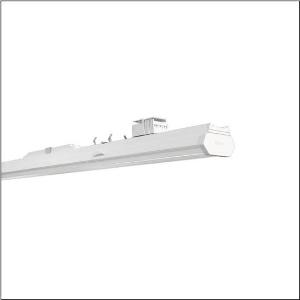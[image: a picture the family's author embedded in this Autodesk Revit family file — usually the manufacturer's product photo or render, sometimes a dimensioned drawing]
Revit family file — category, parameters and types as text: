
# Revit family: licross_11_protected_ho_51tp11cn4exs
name_source: partatom
category: Lighting Fixtures
units: mm (PartAtom-declared; Revit-internal decimal feet)

## family parameters
Cut with Voids When Loaded = No
Host = Face
Light Source = No
Part Type = Normal
Room Calculation Point = No
Round Connector Dimension = Use Diameter
Shared = No

## types (1)
- --- (1 x LED, 14460 lm, 77.6 W, 4000K)
    Apparent Load = 78 VA
    CIE Flux Codes = 84 94 98 99 100
    Color Rendering = 80
    Color Temperature = 4000K
    Default Elevation = 1800 mm
    Description = Licross 11 Protected HO, luminaire insert, of sheet steel, galvanised, coil coated, white, length: 1.500mm, width: 90mm, height: 101mm, LED rated luminous flux: 14.460lm, light colour: 840, SDCM (Standard Deviation of Colour Matching)MacAdam ≤ 2 SDCM (initial), control gear: ON/OFF Multilumen, CLOi, with plug, 3-pole, with phase selection, mains connection: 220..240V, AC, 50/60Hz, start of lifetime: 78W, end of service life: 87W, internal wiring halogen-free, primary light control with lens, of plastic, primary optical cover: cover, of PMMA, light emission: direct distribution, primary light characteristic: symmetric, protection rating (complete): IP64, insulation class (complete): insulation class I (protective earthing), certification: CE, ENEC, VDE, UKCA, protection symbol: D if used in an environment with conductive dust loads with corresponding accessories, impact resistance: IK06, permissible ambient temperature for indoor applications: -35..+35°C, corresponds to IFS (International Featured Standards) requirements for safety and quality in the food industry, reducing of maximum allowable ambient temperature of 5°C with ceiling mounting, LABS conformity tested according to VDMA 24364:2018-05, The light source and the operating device comply with the requirements of the Ecodesign Regulation (EU) 2019/2020 and are replaceable in accordance with this regulation, packaging unit: 1 piece
    Height = 92 mm
    Lamp = 1 x LED
    Lamp Light Flux = 14460 lm
    Lamp Power = 77.6 W
    Lamp count = 1
    Length = 1500 mm
    Luminous efficacy = 186 lm/W
    Manufacturer = Siteco
    ModVariant = No
    Model = 51TP11CN4EXS
    Mounting Place = Ceiling
    Mounting Type = Pendant
    Number of Poles = 1
    OnlyDefault = Yes
    Power Factor = 1
    Product Name = Licross 11 Protected HO
    Product group = luminaire insert | ceiling pendant
    ProductGroupID = 901
    Protection Class = Protection class I
    Protection Degree = IP 64
    RLX_Detail_Level = 1
    RLX_Emergency_Light_Flux = 0 lm
    RLX_Emergency_Type = 0
    RLX_Emergency_Type_DB = No
    RlxData = <blob elided: 22421 chars, md5=ac48fc3c>
    Socket = socket
    Standby Power = 0 W
    System Light Flux = 14460 lm
    System Power = 78 W
    Type Comments = factory setting: luminous flux: 100 % | (A | C | E) | 181 mA
    Type Image = l_1256148.jpg
    URL = http://relux.com
    VarID = @adj_000697
    Voltage = 0 V
    Weight = 0.00 kg
    Width = 88 mm

## geometry (parser evidence)
native form markers: Blend x4, Sweep x12
no freeform markers — native parametric forms only
